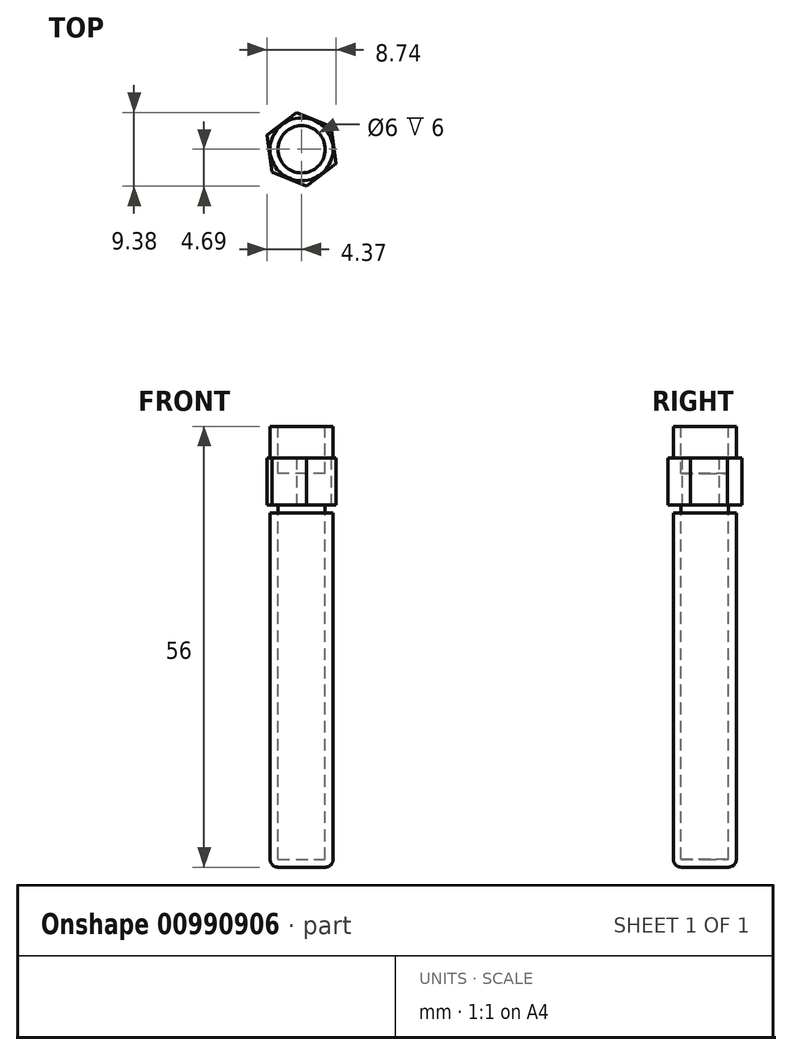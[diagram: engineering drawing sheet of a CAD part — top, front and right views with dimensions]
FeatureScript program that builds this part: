
annotation { "Feature Type Name" : "Feature", "Feature Type Description" : "" }
export const myFeature = defineFeature(function(context is Context, id is Id, definition is map)
    precondition{}
    {
        {
            var Q0;
            Q0=qCreatedBy(makeId("Top.planeOp"),FACE);
            var sketch = newSketch(context, id + "F0", { "sketchPlane" : qUnion([Q0])});
            skCircle(sketch, "E0.cCircle", {"center": v(0, 0) * mm, "radius": 4.1 * mm, "construction": true});
            skLineSegment(sketch, "E0.0", {"start": v(-0.62, 4.7) * mm, "end": v(3.75, 2.88) * mm});
            skLineSegment(sketch, "E0.1", {"start": v(3.75, 2.88) * mm, "end": v(4.37, -1.8) * mm});
            skLineSegment(sketch, "E0.2", {"start": v(4.37, -1.8) * mm, "end": v(0.62, -4.7) * mm});
            skLineSegment(sketch, "E0.3", {"start": v(0.62, -4.7) * mm, "end": v(-3.75, -2.88) * mm});
            skLineSegment(sketch, "E0.4", {"start": v(-3.75, -2.88) * mm, "end": v(-4.37, 1.8) * mm});
            skLineSegment(sketch, "E0.5", {"start": v(-4.37, 1.8) * mm, "end": v(-0.62, 4.7) * mm});
            skPoint(sketch, "E0.0.midPoint", {"position": v(1.57, 3.79) * mm});
            skSolve(sketch);
        }
        {
            var Q0;
            Q0=qSketchRegion(id+"F0",true);
            extrude(context, id + "F1", {"entities" : qUnion([Q0]), "depth" : 6 * mm, "offsetDistance" : 25 * mm});
        }
        {
            var Q0;
            Q0=makeQuery(id+"F1.opExtrude","CAP_FACE",FACE,{"disambiguationData":[OSD([sQuery(id+"F0.wireOp",EDGE,"E0.0"),sQuery(id+"F0.wireOp",EDGE,"E0.1"),sQuery(id+"F0.wireOp",EDGE,"E0.2"),sQuery(id+"F0.wireOp",EDGE,"E0.3"),sQuery(id+"F0.wireOp",EDGE,"E0.4"),sQuery(id+"F0.wireOp",EDGE,"E0.5")])],"isStart":true});
            var sketch = newSketch(context, id + "F2", { "sketchPlane" : qUnion([Q0])});
            skCircle(sketch, "E1", {"center": v(0, 0) * mm, "radius": 3 * mm});
            skSolve(sketch);
        }
        {
            var Q0;
            Q0=qSketchRegion(id+"F2",true);
            extrude(context, id + "F3", {"entities" : qUnion([Q0]), "operationType" : NewBodyOperationType.ADD, "depth" : 45 * mm, "offsetDistance" : 25 * mm});
        }
        {
            var Q0;
            Q0=makeQuery(id+"F1.opExtrude","CAP_FACE",FACE,{"disambiguationData":[OSD([sQuery(id+"F0.wireOp",EDGE,"E0.0"),sQuery(id+"F0.wireOp",EDGE,"E0.1"),sQuery(id+"F0.wireOp",EDGE,"E0.2"),sQuery(id+"F0.wireOp",EDGE,"E0.3"),sQuery(id+"F0.wireOp",EDGE,"E0.4"),sQuery(id+"F0.wireOp",EDGE,"E0.5")])],"isStart":false});
            var sketch = newSketch(context, id + "F4", { "sketchPlane" : qUnion([Q0])});
            skCircle(sketch, "E2", {"center": v(0, 0) * mm, "radius": 4 * mm});
            skSolve(sketch);
        }
        {
            var Q0;
            Q0=qSketchRegion(id+"F4",true);
            extrude(context, id + "F5", {"entities" : qUnion([Q0]), "operationType" : NewBodyOperationType.ADD, "depth" : 4 * mm, "offsetDistance" : 25 * mm});
        }
        {
            var Q0;
            Q0=makeQuery(id+"F5.opExtrude","CAP_FACE",FACE,{"disambiguationData":[OSD([sQuery(id+"F4.wireOp",EDGE,"E2")])],"isStart":false});
            var sketch = newSketch(context, id + "F6", { "sketchPlane" : qUnion([Q0])});
            skCircle(sketch, "E3", {"center": v(0, 0) * mm, "radius": 3 * mm});
            skSolve(sketch);
        }
        {
            var Q0;
            Q0=qSketchRegion(id+"F6",true);
            extrude(context, id + "F7", {"entities" : qUnion([Q0]), "operationType" : NewBodyOperationType.REMOVE, "oppositeDirection" : true, "depth" : 6 * mm, "offsetDistance" : 25 * mm});
        }
        {
            var Q0;
            Q0=qCreatedBy(makeId("Top.planeOp"),FACE);
            cPlane(context, id + "F8", {"entities" : qUnion([Q0]), "cplaneType" : CPlaneType.OFFSET, "offset" : 1 * mm, "oppositeDirection" : true, "width" : 150 * mm, "height" : 150 * mm});
        }
        {
            var Q0;
            Q0=qCreatedBy(id+"F8.planeOp",FACE);
            var sketch = newSketch(context, id + "F9", { "sketchPlane" : qUnion([Q0])});
            skCircle(sketch, "E4", {"center": v(0, 0) * mm, "radius": 4 * mm});
            skSolve(sketch);
        }
        {
            var Q0;
            Q0=qSketchRegion(id+"F9",true);
            extrude(context, id + "F10", {"entities" : qUnion([Q0]), "oppositeDirection" : true, "depth" : 45 * mm, "offsetDistance" : 25 * mm});
        }
        {
            var Q0;
            Q0=makeQuery(id+"F10.opExtrude","CAP_EDGE",EDGE,{"disambiguationData":[OSD([sQuery(id+"F9.wireOp",EDGE,"E4")])],"isStart":false});
            fillet(context, id + "F11", {"entities" : qUnion([Q0]), "radius" : 1 * mm, "tangentPropagation" : true, "allowEdgeOverflow" : false});
        }
    });
